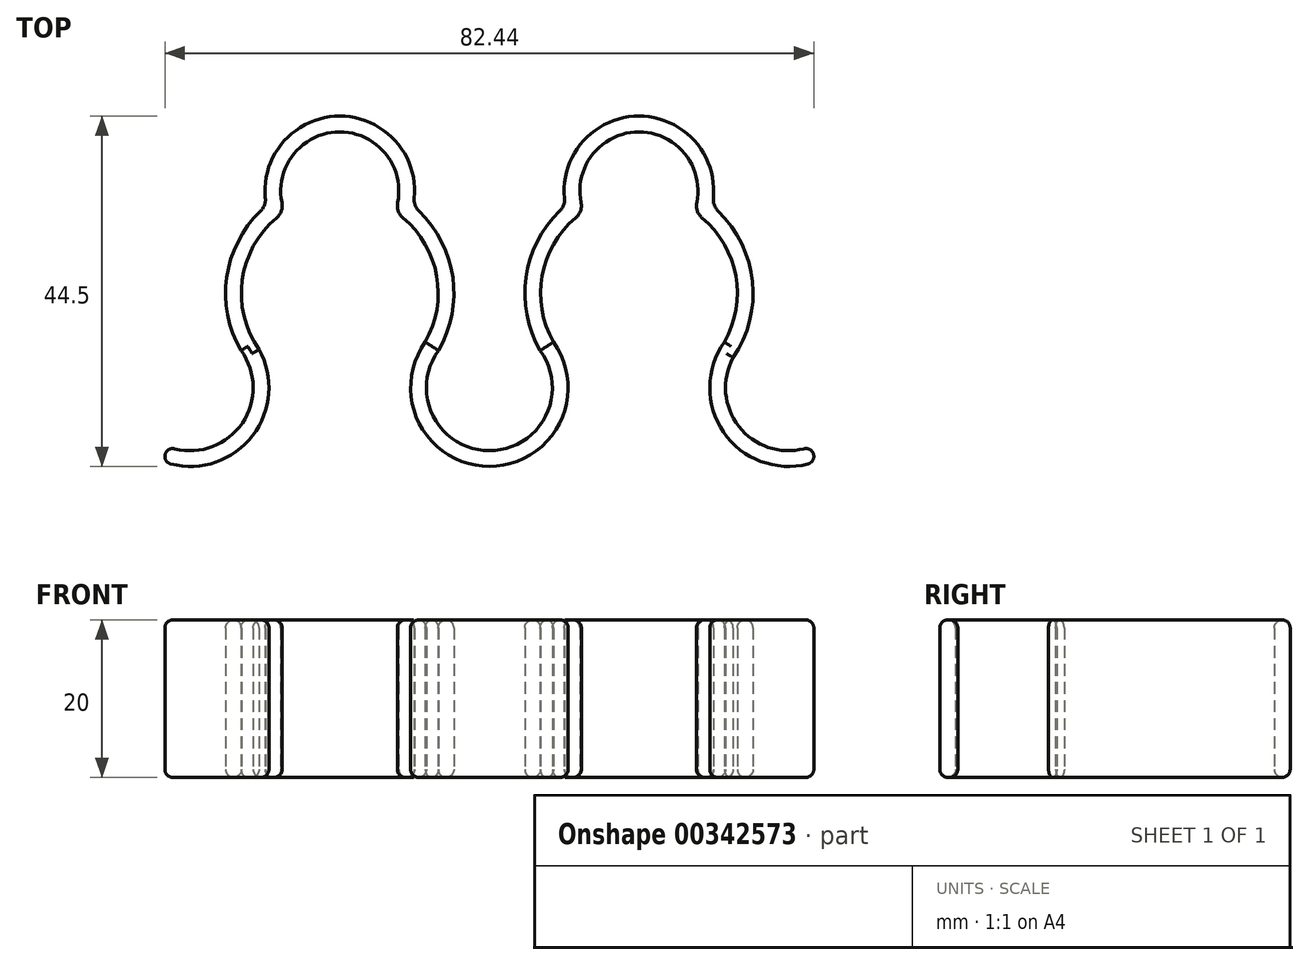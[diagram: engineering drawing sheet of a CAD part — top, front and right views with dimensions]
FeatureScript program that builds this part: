
annotation { "Feature Type Name" : "Feature", "Feature Type Description" : "" }
export const myFeature = defineFeature(function(context is Context, id is Id, definition is map)
    precondition{}
    {
        {
            var Q0;
            Q0=qCreatedBy(makeId("Top.planeOp"),FACE);
            var sketch = newSketch(context, id + "F0", { "sketchPlane" : qUnion([Q0])});
            skArc(sketch, "E0", {"start": v(-6.46, 4.71) * mm, "mid": v(0, -8) * mm, "end": v(6.46, 4.71) * mm});
            skArc(sketch, "E1", {"start": v(-8.15, 5.8) * mm, "mid": v(-8.45, 5.34) * mm, "end": v(-8.74, 4.86) * mm});
            skPoint(sketch, "E2", {"position": v(19, 12) * mm});
            skArc(sketch, "E3", {"start": v(10.97, 21.58) * mm, "mid": v(6.61, 13.66) * mm, "end": v(8.74, 4.86) * mm});
            skArc(sketch, "E4", {"start": v(30.97, 3.8) * mm, "mid": v(33.42, 13.48) * mm, "end": v(29.06, 22.44) * mm});
            skArc(sketch, "E5.MirrorC", {"start": v(-30.97, 3.8) * mm, "mid": v(-33.42, 13.48) * mm, "end": v(-29.06, 22.44) * mm});
            skArc(sketch, "E6.MirrorC", {"start": v(-10.97, 21.58) * mm, "mid": v(-6.61, 13.66) * mm, "end": v(-8.74, 4.86) * mm});
            skArc(sketch, "E7.trimOffspring", {"start": v(8.74, 4.86) * mm, "mid": v(8.45, 5.34) * mm, "end": v(8.15, 5.8) * mm});
            skArc(sketch, "E8.trimOffspring", {"start": v(-8.74, 4.86) * mm, "mid": v(0, -10) * mm, "end": v(8.74, 4.86) * mm});
            skPoint(sketch, "E9", {"position": v(-19, 25) * mm});
            skArc(sketch, "E10", {"start": v(-11.65, 23.51) * mm, "mid": v(-19, 32.5) * mm, "end": v(-26.35, 23.51) * mm});
            skArc(sketch, "E11", {"start": v(-9.54, 24.08) * mm, "mid": v(-19, 34.5) * mm, "end": v(-28.46, 24.08) * mm});
            skArc(sketch, "E12.MirrorC", {"start": v(9.54, 24.08) * mm, "mid": v(19, 34.5) * mm, "end": v(28.46, 24.08) * mm});
            skArc(sketch, "E13.MirrorC", {"start": v(11.65, 23.51) * mm, "mid": v(19, 32.5) * mm, "end": v(26.35, 23.51) * mm});
            skArc(sketch, "E14.trimOffspring", {"start": v(-8.94, 22.44) * mm, "mid": v(-4.58, 13.48) * mm, "end": v(-7.03, 3.8) * mm});
            skArc(sketch, "E15.trimOffspring", {"start": v(8.94, 22.44) * mm, "mid": v(4.58, 13.48) * mm, "end": v(7.03, 3.8) * mm});
            skPoint(sketch, "E16", {"position": v(38, 0) * mm});
            skArc(sketch, "E17", {"start": v(31.54, 4.71) * mm, "mid": v(31.37, -4.48) * mm, "end": v(39.97, -7.75) * mm});
            skArc(sketch, "E18", {"start": v(29.85, 5.8) * mm, "mid": v(29.75, -5.65) * mm, "end": v(40.46, -9.7) * mm});
            skArc(sketch, "E19.MirrorC", {"start": v(-29.85, 5.8) * mm, "mid": v(-29.55, 5.34) * mm, "end": v(-29.26, 4.86) * mm});
            skArc(sketch, "E20.MirrorC", {"start": v(-31.54, 4.71) * mm, "mid": v(-31.37, -4.48) * mm, "end": v(-39.97, -7.75) * mm});
            skArc(sketch, "E21.trimOffspring", {"start": v(-29.26, 4.86) * mm, "mid": v(-30.08, -6.1) * mm, "end": v(-40.46, -9.7) * mm});
            skArc(sketch, "E22.trimOffspring", {"start": v(29.26, 4.86) * mm, "mid": v(31.39, 13.66) * mm, "end": v(27.03, 21.58) * mm});
            skArc(sketch, "E23.trimOffspring", {"start": v(-29.26, 4.86) * mm, "mid": v(-31.39, 13.66) * mm, "end": v(-27.03, 21.58) * mm});
            skLineSegment(sketch, "E24", {"start": v(-41.22, -8.72) * mm, "end": v(-41.22, -8.72) * mm});
            skLineSegment(sketch, "E25", {"start": v(41.22, -8.72) * mm, "end": v(41.22, -8.72) * mm});
            skPoint(sketch, "E26.visualSharp", {"position": v(-26.01, 22.35) * mm});
            skArc(sketch, "E26.filletArc", {"start": v(-27.03, 21.58) * mm, "mid": v(-26.42, 22.45) * mm, "end": v(-26.35, 23.51) * mm});
            skPoint(sketch, "E27.visualSharp", {"position": v(-11.99, 22.35) * mm});
            skArc(sketch, "E27.filletArc", {"start": v(-11.65, 23.51) * mm, "mid": v(-11.58, 22.45) * mm, "end": v(-10.97, 21.58) * mm});
            skPoint(sketch, "E28.visualSharp", {"position": v(11.99, 22.35) * mm});
            skArc(sketch, "E28.filletArc", {"start": v(10.97, 21.58) * mm, "mid": v(11.58, 22.45) * mm, "end": v(11.65, 23.51) * mm});
            skPoint(sketch, "E29.visualSharp", {"position": v(26.01, 22.35) * mm});
            skArc(sketch, "E29.filletArc", {"start": v(26.35, 23.51) * mm, "mid": v(26.42, 22.45) * mm, "end": v(27.03, 21.58) * mm});
            skArc(sketch, "E30.filletArc", {"start": v(-9.54, 24.08) * mm, "mid": v(-9.43, 23.2) * mm, "end": v(-8.94, 22.44) * mm});
            skArc(sketch, "E31.filletArc", {"start": v(-29.06, 22.44) * mm, "mid": v(-28.57, 23.2) * mm, "end": v(-28.46, 24.08) * mm});
            skArc(sketch, "E32.filletArc", {"start": v(8.94, 22.44) * mm, "mid": v(9.43, 23.2) * mm, "end": v(9.54, 24.08) * mm});
            skArc(sketch, "E33.filletArc", {"start": v(28.46, 24.08) * mm, "mid": v(28.57, 23.2) * mm, "end": v(29.06, 22.44) * mm});
            skPoint(sketch, "E34.visualSharp", {"position": v(-41.22, -7.32) * mm});
            skArc(sketch, "E34.filletArc", {"start": v(-39.97, -7.75) * mm, "mid": v(-40.83, -7.93) * mm, "end": v(-41.22, -8.72) * mm});
            skPoint(sketch, "E35.visualSharp", {"position": v(-41.22, -9.47) * mm});
            skArc(sketch, "E35.filletArc", {"start": v(-41.22, -8.72) * mm, "mid": v(-41, -9.34) * mm, "end": v(-40.46, -9.7) * mm});
            skPoint(sketch, "E36.visualSharp", {"position": v(41.22, -7.32) * mm});
            skArc(sketch, "E36.filletArc", {"start": v(41.22, -8.72) * mm, "mid": v(40.83, -7.93) * mm, "end": v(39.97, -7.75) * mm});
            skPoint(sketch, "E37.visualSharp", {"position": v(41.22, -9.47) * mm});
            skArc(sketch, "E37.filletArc", {"start": v(40.46, -9.7) * mm, "mid": v(41, -9.34) * mm, "end": v(41.22, -8.72) * mm});
            skSolve(sketch);
        }
        {
            var Q0;
            {var subQ26=sQuery(id+"F0.wireOp",EDGE,"E8.trimOffspring");Q0=makeQuery(id+"F0.imprint","IMPRINT",FACE,{"disambiguationData":[TD([[makeQuery(id+"F0.imprint","IMPRINT",EDGE,{"derivedFrom":subQ26}),1.0]])]});}
            var Q1;
            {var subQ0=sQuery(id+"F0.wireOp",EDGE,"E20.MirrorC");var subQ1=sQuery(id+"F0.wireOp",EDGE,"E5.MirrorC");var subQ2=makeQuery(id+"F0.imprint","INTERSECT",VERTEX,{"disambiguationData":[OD(0.0)],"derivedFrom":[subQ1,subQ0]});Q1=makeQuery(id+"F0.imprint","IMPRINT",FACE,{"disambiguationData":[TD([[makeQuery(id+"F0.imprint","IMPRINT",EDGE,{"disambiguationData":[TD([[subQ2,-1.0]])],"derivedFrom":subQ1}),-1.0]])]});}
            var Q2;
            {var subQ0=sQuery(id+"F0.wireOp",EDGE,"E15.trimOffspring");var subQ1=sQuery(id+"F0.wireOp",EDGE,"E0");var subQ2=makeQuery(id+"F0.imprint","INTERSECT",VERTEX,{"disambiguationData":[OD(0.0)],"derivedFrom":[subQ1,subQ0]});Q2=makeQuery(id+"F0.imprint","IMPRINT",FACE,{"disambiguationData":[TD([[makeQuery(id+"F0.imprint","IMPRINT",EDGE,{"disambiguationData":[TD([[subQ2,1.0]])],"derivedFrom":subQ1}),1.0]])]});}
            var Q3;
            {var subQ0=sQuery(id+"F0.wireOp",EDGE,"E14.trimOffspring");var subQ1=sQuery(id+"F0.wireOp",EDGE,"E0");var subQ2=makeQuery(id+"F0.imprint","INTERSECT",VERTEX,{"disambiguationData":[OD(0.0)],"derivedFrom":[subQ1,subQ0]});Q3=makeQuery(id+"F0.imprint","IMPRINT",FACE,{"disambiguationData":[TD([[makeQuery(id+"F0.imprint","IMPRINT",EDGE,{"disambiguationData":[TD([[subQ2,-1.0]])],"derivedFrom":subQ1}),1.0]])]});}
            var Q4;
            {var subQ0=sQuery(id+"F0.wireOp",EDGE,"E22.trimOffspring");var subQ1=sQuery(id+"F0.wireOp",EDGE,"E18");var subQ2=makeQuery(id+"F0.imprint","INTERSECT",VERTEX,{"disambiguationData":[OD(0.0)],"derivedFrom":[subQ1,subQ0]});Q4=makeQuery(id+"F0.imprint","IMPRINT",FACE,{"disambiguationData":[TD([[makeQuery(id+"F0.imprint","IMPRINT",EDGE,{"disambiguationData":[TD([[subQ2,-1.0]])],"derivedFrom":subQ1}),1.0]])]});}
            var Q5;
            {var subQ0=sQuery(id+"F0.wireOp",EDGE,"E17");var subQ1=sQuery(id+"F0.wireOp",EDGE,"E4");var subQ2=makeQuery(id+"F0.imprint","INTERSECT",VERTEX,{"disambiguationData":[OD(0.0)],"derivedFrom":[subQ1,subQ0]});Q5=makeQuery(id+"F0.imprint","IMPRINT",FACE,{"disambiguationData":[TD([[makeQuery(id+"F0.imprint","IMPRINT",EDGE,{"disambiguationData":[TD([[subQ2,-1.0]])],"derivedFrom":subQ1}),1.0]])]});}
            var Q6;
            {var subQ0=sQuery(id+"F0.wireOp",EDGE,"E1");Q6=makeQuery(id+"F0.imprint","IMPRINT",FACE,{"disambiguationData":[TD([[makeQuery(id+"F0.imprint","IMPRINT",EDGE,{"derivedFrom":subQ0}),1.0]])]});}
            var Q7;
            {var subQ0=sQuery(id+"F0.wireOp",EDGE,"E7.trimOffspring");Q7=makeQuery(id+"F0.imprint","IMPRINT",FACE,{"disambiguationData":[TD([[makeQuery(id+"F0.imprint","IMPRINT",EDGE,{"derivedFrom":subQ0}),1.0]])]});}
            var Q8;
            {var subQ0=sQuery(id+"F0.wireOp",EDGE,"E19.MirrorC");Q8=makeQuery(id+"F0.imprint","IMPRINT",FACE,{"disambiguationData":[TD([[makeQuery(id+"F0.imprint","IMPRINT",EDGE,{"derivedFrom":subQ0}),-1.0]])]});}
            extrude(context, id + "F1", {"entities" : qUnion([Q0, Q1, Q2, Q3, Q4, Q5, Q6, Q7, Q8]), "depth" : 20 * mm});
        }
        {
            var Q0;
            Q0=makeQuery(id+"F1.opExtrude","CAP_FACE",FACE,{"disambiguationData":[OSD([sQuery(id+"F0.wireOp",EDGE,"E0"),sQuery(id+"F0.wireOp",EDGE,"E1"),sQuery(id+"F0.wireOp",EDGE,"E3"),sQuery(id+"F0.wireOp",EDGE,"E4"),sQuery(id+"F0.wireOp",EDGE,"E5.MirrorC"),sQuery(id+"F0.wireOp",EDGE,"E6.MirrorC"),sQuery(id+"F0.wireOp",EDGE,"E7.trimOffspring"),sQuery(id+"F0.wireOp",EDGE,"E8.trimOffspring"),sQuery(id+"F0.wireOp",EDGE,"E10"),sQuery(id+"F0.wireOp",EDGE,"E11"),sQuery(id+"F0.wireOp",EDGE,"E12.MirrorC"),sQuery(id+"F0.wireOp",EDGE,"E13.MirrorC"),sQuery(id+"F0.wireOp",EDGE,"E14.trimOffspring"),sQuery(id+"F0.wireOp",EDGE,"E15.trimOffspring"),sQuery(id+"F0.wireOp",EDGE,"E17"),sQuery(id+"F0.wireOp",EDGE,"E18"),sQuery(id+"F0.wireOp",EDGE,"E19.MirrorC"),sQuery(id+"F0.wireOp",EDGE,"E20.MirrorC"),sQuery(id+"F0.wireOp",EDGE,"E21.trimOffspring"),sQuery(id+"F0.wireOp",EDGE,"E22.trimOffspring"),sQuery(id+"F0.wireOp",EDGE,"E23.trimOffspring"),sQuery(id+"F0.wireOp",EDGE,"E26.filletArc"),sQuery(id+"F0.wireOp",EDGE,"E27.filletArc"),sQuery(id+"F0.wireOp",EDGE,"E28.filletArc"),sQuery(id+"F0.wireOp",EDGE,"E29.filletArc"),sQuery(id+"F0.wireOp",EDGE,"E30.filletArc"),sQuery(id+"F0.wireOp",EDGE,"E31.filletArc"),sQuery(id+"F0.wireOp",EDGE,"E32.filletArc"),sQuery(id+"F0.wireOp",EDGE,"E33.filletArc"),sQuery(id+"F0.wireOp",EDGE,"E34.filletArc"),sQuery(id+"F0.wireOp",EDGE,"E35.filletArc"),sQuery(id+"F0.wireOp",EDGE,"E36.filletArc"),sQuery(id+"F0.wireOp",EDGE,"E37.filletArc")])],"isStart":false});
            fillet(context, id + "F2", {"entities" : qUnion([Q0]), "radius" : 1 * mm, "tangentPropagation" : true, "allowEdgeOverflow" : false});
        }
        {
            var Q0;
            Q0=makeQuery(id+"F1.opExtrude","CAP_FACE",FACE,{"disambiguationData":[OSD([sQuery(id+"F0.wireOp",EDGE,"E0"),sQuery(id+"F0.wireOp",EDGE,"E1"),sQuery(id+"F0.wireOp",EDGE,"E3"),sQuery(id+"F0.wireOp",EDGE,"E4"),sQuery(id+"F0.wireOp",EDGE,"E5.MirrorC"),sQuery(id+"F0.wireOp",EDGE,"E6.MirrorC"),sQuery(id+"F0.wireOp",EDGE,"E7.trimOffspring"),sQuery(id+"F0.wireOp",EDGE,"E8.trimOffspring"),sQuery(id+"F0.wireOp",EDGE,"E10"),sQuery(id+"F0.wireOp",EDGE,"E11"),sQuery(id+"F0.wireOp",EDGE,"E12.MirrorC"),sQuery(id+"F0.wireOp",EDGE,"E13.MirrorC"),sQuery(id+"F0.wireOp",EDGE,"E14.trimOffspring"),sQuery(id+"F0.wireOp",EDGE,"E15.trimOffspring"),sQuery(id+"F0.wireOp",EDGE,"E17"),sQuery(id+"F0.wireOp",EDGE,"E18"),sQuery(id+"F0.wireOp",EDGE,"E19.MirrorC"),sQuery(id+"F0.wireOp",EDGE,"E20.MirrorC"),sQuery(id+"F0.wireOp",EDGE,"E21.trimOffspring"),sQuery(id+"F0.wireOp",EDGE,"E22.trimOffspring"),sQuery(id+"F0.wireOp",EDGE,"E23.trimOffspring"),sQuery(id+"F0.wireOp",EDGE,"E26.filletArc"),sQuery(id+"F0.wireOp",EDGE,"E27.filletArc"),sQuery(id+"F0.wireOp",EDGE,"E28.filletArc"),sQuery(id+"F0.wireOp",EDGE,"E29.filletArc"),sQuery(id+"F0.wireOp",EDGE,"E30.filletArc"),sQuery(id+"F0.wireOp",EDGE,"E31.filletArc"),sQuery(id+"F0.wireOp",EDGE,"E32.filletArc"),sQuery(id+"F0.wireOp",EDGE,"E33.filletArc"),sQuery(id+"F0.wireOp",EDGE,"E34.filletArc"),sQuery(id+"F0.wireOp",EDGE,"E35.filletArc"),sQuery(id+"F0.wireOp",EDGE,"E36.filletArc"),sQuery(id+"F0.wireOp",EDGE,"E37.filletArc")])],"isStart":true});
            fillet(context, id + "F3", {"entities" : qUnion([Q0]), "radius" : 1 * mm, "tangentPropagation" : true, "allowEdgeOverflow" : false});
        }
    });
